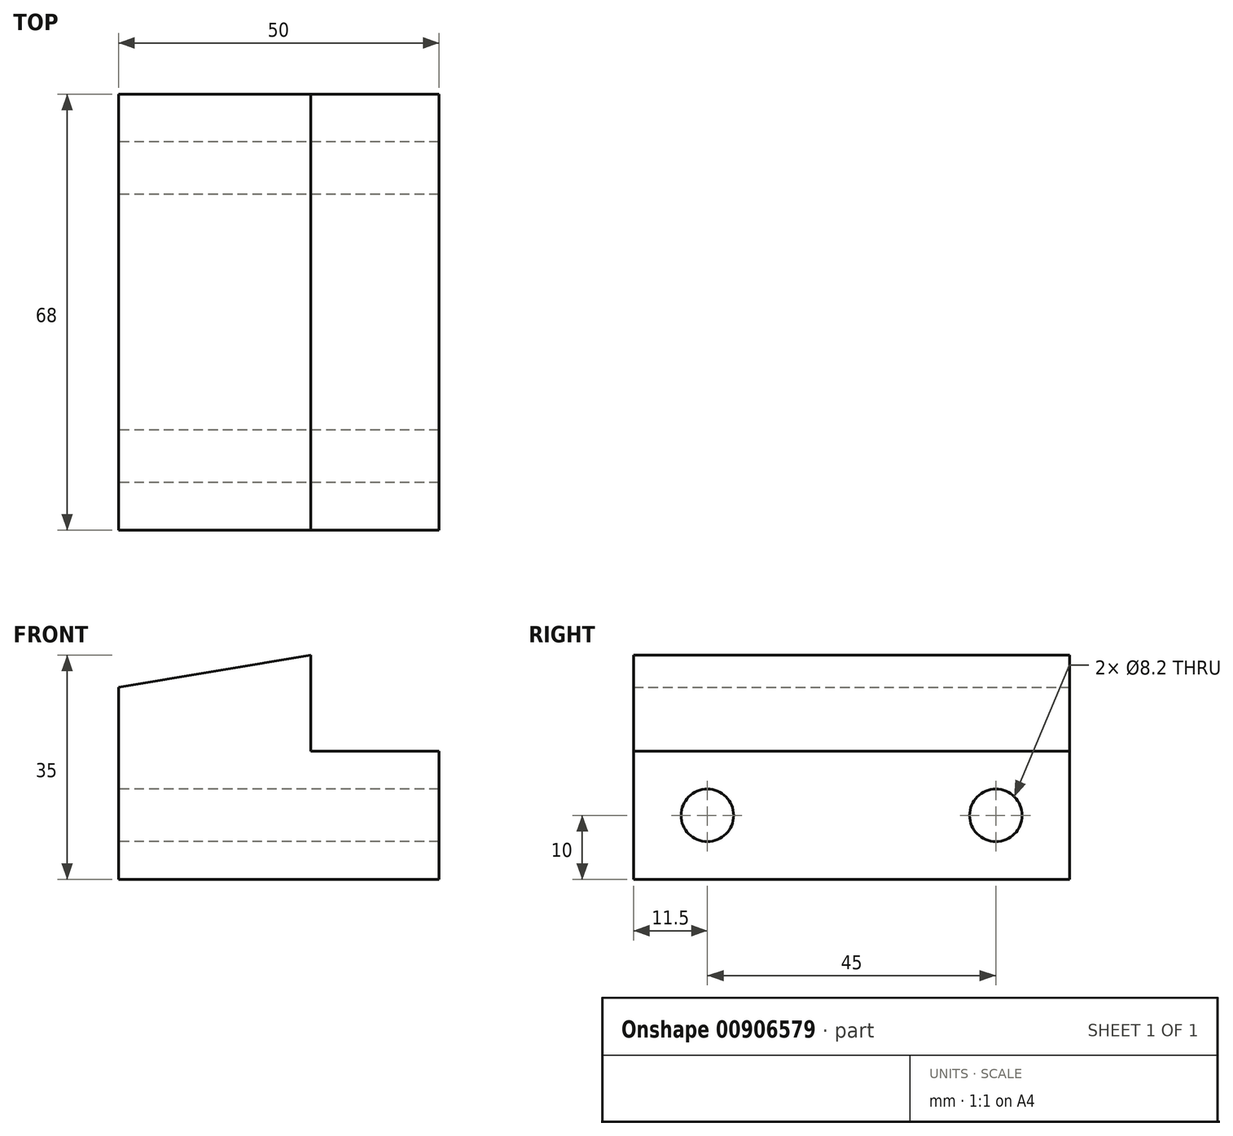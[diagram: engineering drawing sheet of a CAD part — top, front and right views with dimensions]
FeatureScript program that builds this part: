
annotation { "Feature Type Name" : "Feature", "Feature Type Description" : "" }
export const myFeature = defineFeature(function(context is Context, id is Id, definition is map)
    precondition{}
    {
        {
            var Q0;
            Q0=qCreatedBy(makeId("Front.planeOp"),FACE);
            var sketch = newSketch(context, id + "F0", { "sketchPlane" : qUnion([Q0])});
            skLineSegment(sketch, "E0", {"start": v(0, 0) * mm, "end": v(50, 0) * mm});
            skLineSegment(sketch, "E1", {"start": v(50, 0) * mm, "end": v(50, 20) * mm});
            skLineSegment(sketch, "E2", {"start": v(50, 20) * mm, "end": v(30, 20) * mm});
            skLineSegment(sketch, "E3", {"start": v(30, 20) * mm, "end": v(30, 35) * mm});
            skLineSegment(sketch, "E4", {"start": v(30, 35) * mm, "end": v(0, 30) * mm});
            skLineSegment(sketch, "E5", {"start": v(0, 30) * mm, "end": v(0, 0) * mm});
            skSolve(sketch);
        }
        {
            var Q0;
            Q0 = qSketchRegion(id + "F0", true);
            extrude(context, id + "F1", {"entities" : qUnion([Q0]), "endBound" : BoundingType.SYMMETRIC, "depth" : 68 * mm, "offsetDistance" : 25 * mm});
        }
        {
            var Q0;
            Q0=makeQuery(id+"F1.opExtrude","SWEPT_FACE",FACE,{"disambiguationData":[OSD([sQuery(id+"F0.wireOp",EDGE,"E5")])]});
            var sketch = newSketch(context, id + "F2", { "sketchPlane" : qUnion([Q0])});
            skPoint(sketch, "E6", {"position": v(-22.5, 10) * mm});
            skPoint(sketch, "E7", {"position": v(22.5, 10) * mm});
            skLineSegment(sketch, "E8", {"start": v(0, 0) * mm, "end": v(0, 24.69) * mm, "construction": true});
            skSolve(sketch);
        }
        {
            var Q0;
            Q0=sQuery(id+"F2.wireOp",VERTEX,"E6");
            var Q1;
            Q1=sQuery(id+"F2.wireOp",VERTEX,"E7");
            var Q2;
            Q2=makeQuery(id+"F1.opExtrude","SWEPT_BODY",BODY,{"disambiguationData":[OSD([sQuery(id+"F0.wireOp",EDGE,"E0"),sQuery(id+"F0.wireOp",EDGE,"E1"),sQuery(id+"F0.wireOp",EDGE,"E2"),sQuery(id+"F0.wireOp",EDGE,"E3"),sQuery(id+"F0.wireOp",EDGE,"E4"),sQuery(id+"F0.wireOp",EDGE,"E5")])]});
            hole(context, id + "F3", {"style" : HoleStyle.SIMPLE, "endStyle" : HoleEndStyle.THROUGH, "standardTappedOrClearance" : lookupTablePath({ "standard" : "ISO", "size" : "8.2", "type" : "Drilled" }), "standardBlindInLast" : lookupTablePath({ "standard" : "ISO", "size" : "8.2", "type" : "Drilled" }), "holeDiameter" : 8.2 * mm, "majorDiameter" : 5 * mm, "isTappedThrough" : true, "tappedDepth" : 12 * mm, "tapClearance" : 3, "locations" : qUnion([Q0, Q1]), "scope" : qUnion([Q2])});
        }
    });
